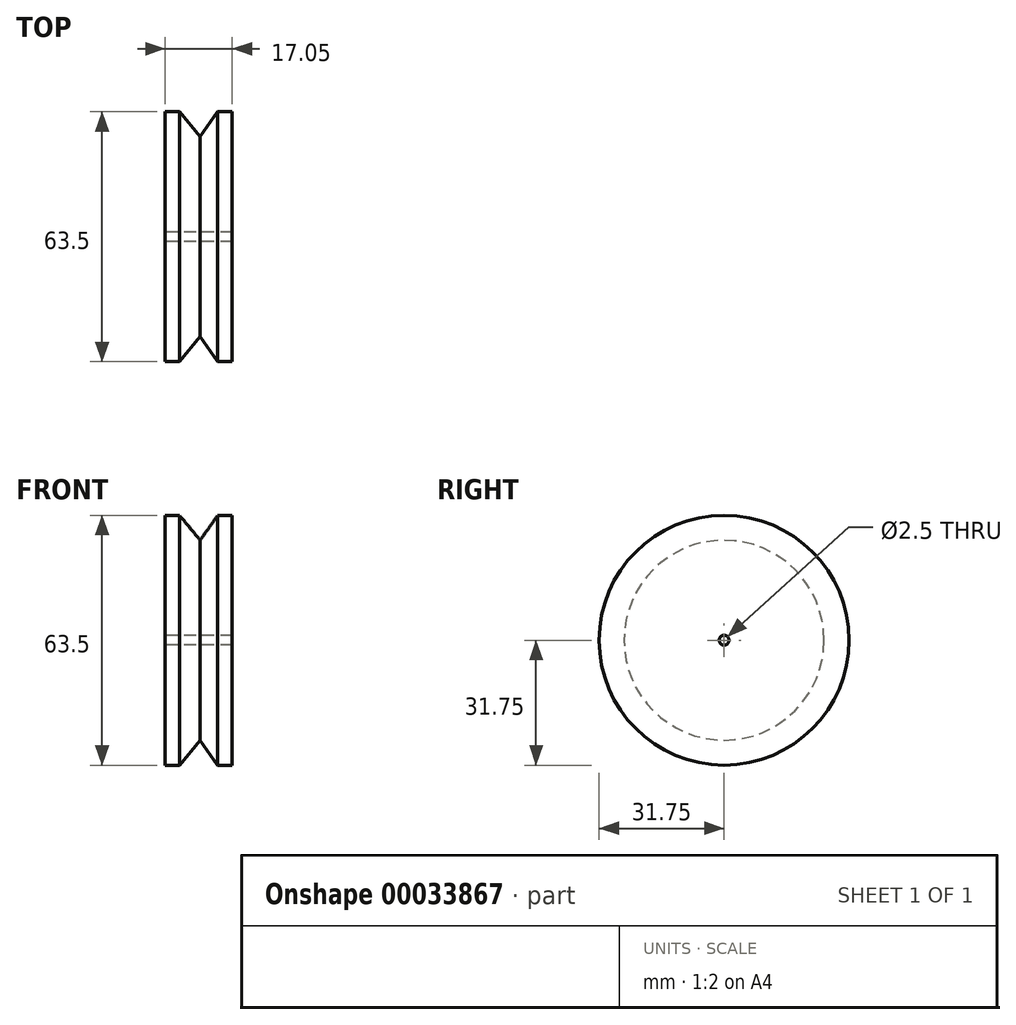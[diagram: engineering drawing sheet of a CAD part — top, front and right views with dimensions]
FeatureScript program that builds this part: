
annotation { "Feature Type Name" : "Feature", "Feature Type Description" : "" }
export const myFeature = defineFeature(function(context is Context, id is Id, definition is map)
    precondition{}
    {
        {
            var Q0;
            Q0=qCreatedBy(makeId("Front.planeOp"),FACE);
            var sketch = newSketch(context, id + "F0", { "sketchPlane" : qUnion([Q0])});
            skLineSegment(sketch, "E0", {"start": v(-8.93, 0) * mm, "end": v(-8.93, 31.75) * mm});
            skLineSegment(sketch, "E1", {"start": v(-8.93, 31.75) * mm, "end": v(-5.27, 31.75) * mm});
            skLineSegment(sketch, "E2", {"start": v(0, 25.4) * mm, "end": v(4.46, 31.75) * mm});
            skLineSegment(sketch, "E3", {"start": v(4.46, 31.75) * mm, "end": v(8.12, 31.75) * mm});
            skLineSegment(sketch, "E4", {"start": v(8.12, 31.75) * mm, "end": v(8.12, 0) * mm});
            skLineSegment(sketch, "E5", {"start": v(8.12, 0) * mm, "end": v(-8.93, 0) * mm});
            skLineSegment(sketch, "E6", {"start": v(25.91, 0) * mm, "end": v(38.83, 0) * mm, "construction": true});
            skLineSegment(sketch, "E7", {"start": v(-5.27, 31.75) * mm, "end": v(0, 25.4) * mm});
            skSolve(sketch);
        }
        {
            var Q0;
            Q0=makeQuery(id+"F0.imprint","IMPRINT",FACE,{"disambiguationData":[TD([[makeQuery(id+"F0.imprint","IMPRINT",EDGE,{"derivedFrom":sQuery(id+"F0.wireOp",EDGE,"E0")}),-1.0]])]});
            var Q1;
            Q1=sQuery(id+"F0.wireOp",EDGE,"E0");
            var Q2;
            Q2=sQuery(id+"F0.wireOp",EDGE,"E1");
            var Q3;
            Q3=sQuery(id+"F0.wireOp",EDGE,"389dfc50-abc8-4249-be2e-4d6fde75a983");
            var Q4;
            Q4=sQuery(id+"F0.wireOp",EDGE,"E3");
            var Q5;
            Q5=sQuery(id+"F0.wireOp",EDGE,"E4");
            var Q6;
            Q6=sQuery(id+"F0.wireOp",EDGE,"E2");
            var Q7;
            Q7=sQuery(id+"F0.wireOp",EDGE,"0de2c3a8-fd2b-4f43-8416-fdfe2e81005f");
            var Q8;
            Q8=sQuery(id+"F0.wireOp",EDGE,"E6");
            revolve(context, id + "F1", {"entities" : qUnion([Q0]), "surfaceEntities" : qUnion([Q1, Q2, Q3, Q4, Q5, Q6, Q7]), "axis" : qUnion([Q8]), "revolveType" : RevolveType.FULL});
        }
        {
            var Q0;
            Q0=qCreatedBy(makeId("Right.planeOp"),FACE);
            var sketch = newSketch(context, id + "F2", { "sketchPlane" : qUnion([Q0])});
            skCircle(sketch, "E8", {"center": v(0, 0) * mm, "radius": 1.25 * mm});
            skSolve(sketch);
        }
        {
            var Q0;
            Q0=makeQuery(id+"F2.imprint","IMPRINT",FACE,{"disambiguationData":[TD([[makeQuery(id+"F2.imprint","IMPRINT",EDGE,{"derivedFrom":sQuery(id+"F2.wireOp",EDGE,"E8")}),1.0]])]});
            extrude(context, id + "F3", {"entities" : qUnion([Q0]), "operationType" : NewBodyOperationType.REMOVE, "depth" : 20.27 * mm, "hasSecondDirection" : true, "secondDirectionOppositeDirection" : true, "secondDirectionDepth" : 25.4 * mm});
        }
    });
